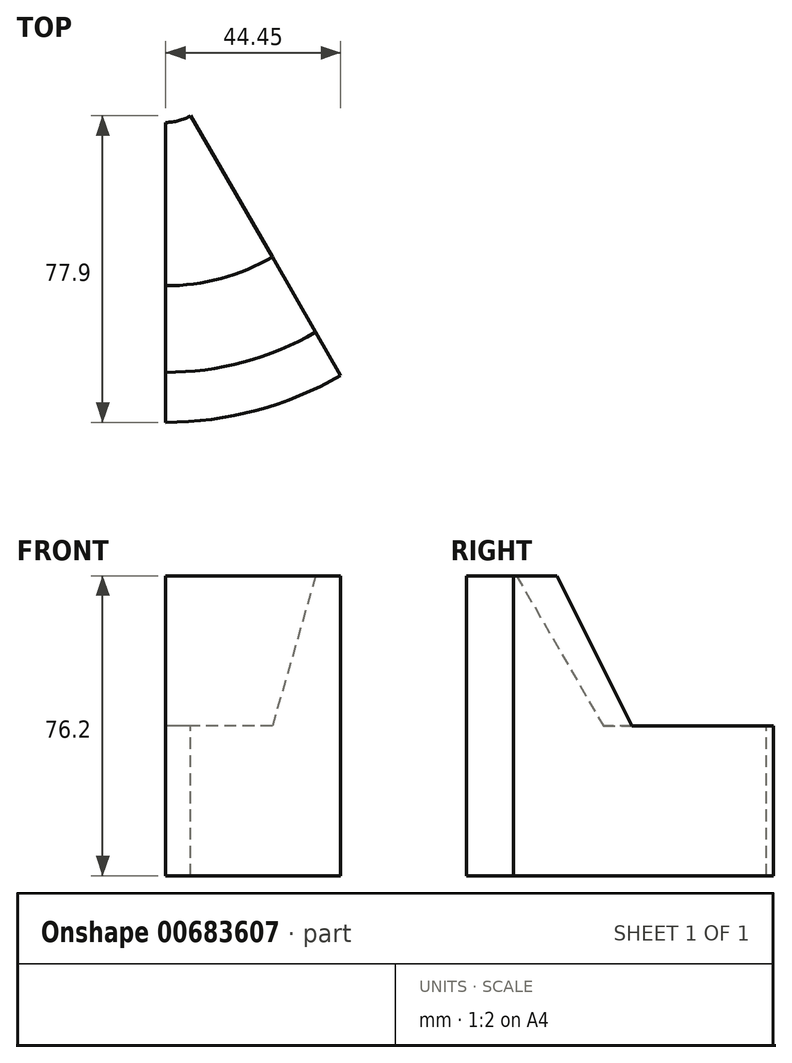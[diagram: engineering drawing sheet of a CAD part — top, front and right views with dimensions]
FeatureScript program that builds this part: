
annotation { "Feature Type Name" : "Feature", "Feature Type Description" : "" }
export const myFeature = defineFeature(function(context is Context, id is Id, definition is map)
    precondition{}
    {
        {
            var Q0;
            Q0=qCreatedBy(makeId("Right.planeOp"),FACE);
            var sketch = newSketch(context, id + "F0", { "sketchPlane" : qUnion([Q0])});
            skLineSegment(sketch, "E0.bottom", {"start": v(-12.7, 0) * mm, "end": v(-88.9, 0) * mm});
            skLineSegment(sketch, "E0.top", {"start": v(-76.2, 76.2) * mm, "end": v(-88.9, 76.2) * mm});
            skLineSegment(sketch, "E0.left", {"start": v(-12.7, 0) * mm, "end": v(-12.7, 38.1) * mm});
            skLineSegment(sketch, "E0.right", {"start": v(-88.9, 0) * mm, "end": v(-88.9, 76.2) * mm});
            skLineSegment(sketch, "E1", {"start": v(-76.2, 76.2) * mm, "end": v(-54.2, 38.1) * mm});
            skLineSegment(sketch, "E2", {"start": v(-54.2, 38.1) * mm, "end": v(-12.7, 38.1) * mm});
            skLineSegment(sketch, "E3", {"start": v(0, 0) * mm, "end": v(0, 42.14) * mm});
            skSolve(sketch);
        }
        {
            var Q0;
            Q0=makeQuery(id+"F0.imprint","IMPRINT",FACE,{"disambiguationData":[TD([[makeQuery(id+"F0.imprint","IMPRINT",EDGE,{"derivedFrom":sQuery(id+"F0.wireOp",EDGE,"E0.bottom")}),-1.0]])]});
            var Q1;
            Q1=sQuery(id+"F0.wireOp",EDGE,"E3");
            revolve(context, id + "F1", {"entities" : qUnion([Q0]), "axis" : qUnion([Q1]), "revolveType" : RevolveType.ONE_DIRECTION, "angle" : 30 * degree});
        }
    });
